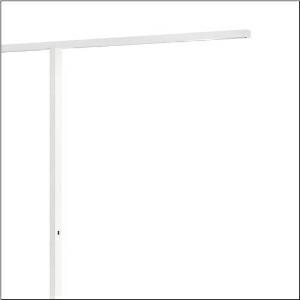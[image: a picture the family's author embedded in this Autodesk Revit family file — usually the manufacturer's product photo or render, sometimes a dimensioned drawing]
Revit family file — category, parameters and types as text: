
# Revit family: silica_r__11_floor_duo_5mx51bs8wzk00006xx_4f95
name_source: partatom
category: Lighting Fixtures
units: mm (PartAtom-declared; Revit-internal decimal feet)

## family parameters
Cut with Voids When Loaded = No
Host = Face
Light Source = No
Part Type = Normal
Room Calculation Point = No
Round Connector Dimension = Use Diameter
Shared = No

## types (1)
- --- (1 x LED, 3970 lm / 8500 lm, 24.1 W / 53.2 W, 4000K)
    Apparent Load = 155 VA
    CIE Flux Codes = 82 97 100 100 100 / - - - 0 100
    Color Rendering = 80
    Color Temperature = 4000K
    Default Elevation = 1800 mm
    Description = Silica® 11 Floor duo, floorstanding luminaire, of PMMA, primary optical cover: cover panel, of PMMA, light emission: indirect/direct distribution, primary light characteristic: symmetric, installation type: not mounted, LED, rated luminous flux: 24.930lm, luminous efficacy: 161lm/W, light colour: 840, colour temperature: 4000K, control gear: DALI, daylight-dependent control, mains connection: 230V, AC, 50Hz, connection cable pre-assembled, cable length: 3m, rated input power: 155W, luminaire head, rectangular, rounded, of aluminium, coated, traffic white (RAL 9016), supporting column, angular, of aluminium, coated, traffic white (RAL 9016), baseplate, of steel, coated, traffic white (RAL 9016), length: 2.598mm, width: 65mm, protection rating (complete): IP20, insulation class (complete): insulation class I (protective earthing), certification: CE, permissible operating ambient temperature: 0..+35°C, standard: EN 50419, packaging unit: 1 piece
    Height = 40 mm  [stored 0.131234 ft]
    Lamp = 1 x LED
    Lamp Light Flux = 3970 lm / 8500 lm
    Lamp Power = 24.1 W / 53.2 W
    Lamp count = 1
    Length = 2598 mm
    Luminous efficacy = 161 lm/W
    Manufacturer = Siteco
    ModVariant = No
    Model = 5MX51BS8WZK00006XX
    Mounting Place = Floor
    Mounting Type = Freestanding
    Number of Poles = 1
    OnlyDefault = Yes
    Power Factor = 1
    Product Name = Silica® 11 Floor duo
    Product group = floorstanding luminaire
    ProductGroupID = 1302
    Protection Class = Protection class I
    Protection Degree = IP 20
    RLX_Detail_Level = 1
    RLX_Emergency_Light_Flux = 0 lm
    RLX_Emergency_Type = 0
    RLX_Emergency_Type_DB = No
    RlxData = <blob elided: 19181 chars, md5=002f8da5>
    Socket = socket
    Standby Power = 0 W
    System Light Flux = 24940 lm
    System Power = 155 W
    Type Comments = factory setting: direct and indirect light
    Type Image = l_1004652.jpg
    URL = http://relux.com
    VarID = @adj_219539
    Voltage = 0 V
    Weight = 0.00 kg
    Width = 65 mm

note: [stored X ft] marks values corroborated as IEEE doubles in the binary element streams (Revit-internal decimal feet)

## geometry (parser evidence)
native form markers: Blend x4, Sweep x18
no freeform markers — native parametric forms only
